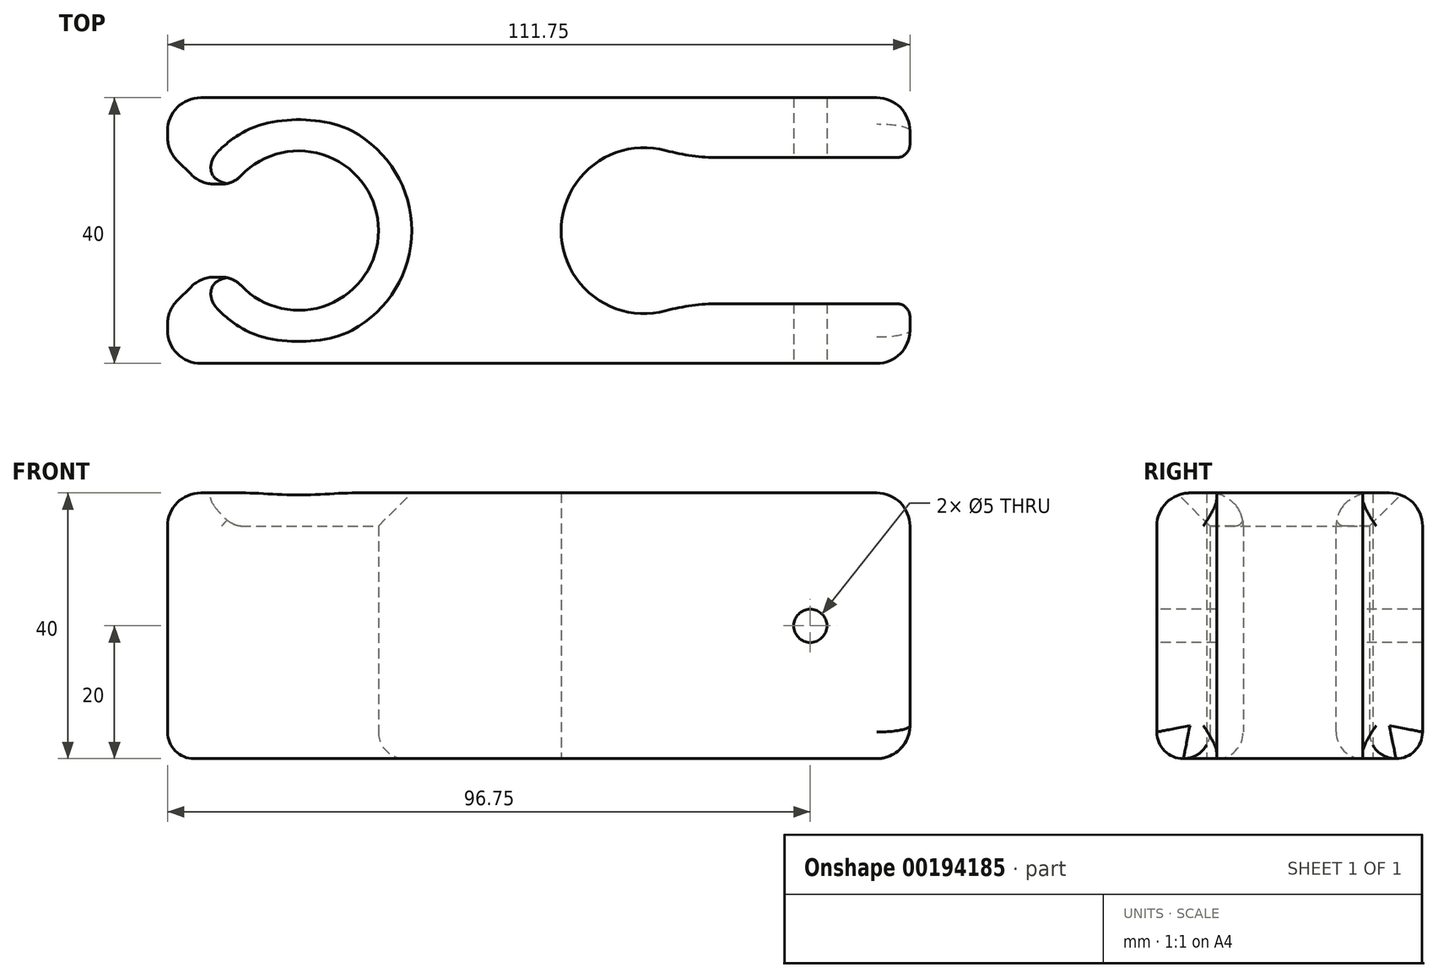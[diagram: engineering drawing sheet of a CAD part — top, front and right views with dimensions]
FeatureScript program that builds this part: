
annotation { "Feature Type Name" : "Feature", "Feature Type Description" : "" }
export const myFeature = defineFeature(function(context is Context, id is Id, definition is map)
    precondition{}
    {
        {
            var Q0;
            Q0=qCreatedBy(makeId("Top.planeOp"),FACE);
            var sketch = newSketch(context, id + "F0", { "sketchPlane" : qUnion([Q0])});
            skArc(sketch, "E0", {"start": v(5.94, 11) * mm, "mid": v(-12.5, 0) * mm, "end": v(5.94, -11) * mm});
            skLineSegment(sketch, "E1", {"start": v(0, 20) * mm, "end": v(40, 20) * mm});
            skLineSegment(sketch, "E2", {"start": v(40, 20) * mm, "end": v(40, 11) * mm});
            skLineSegment(sketch, "E3", {"start": v(40, 11) * mm, "end": v(5.94, 11) * mm});
            skLineSegment(sketch, "E4.MirrorCS", {"start": v(0, -20) * mm, "end": v(40, -20) * mm});
            skLineSegment(sketch, "E5.MirrorCS", {"start": v(40, -20) * mm, "end": v(40, -11) * mm});
            skLineSegment(sketch, "E6.MirrorCS", {"start": v(40, -11) * mm, "end": v(5.94, -11) * mm});
            skLineSegment(sketch, "E7", {"start": v(0, 20) * mm, "end": v(-61.8, 20) * mm});
            skLineSegment(sketch, "E8", {"start": v(-64, -20) * mm, "end": v(0, -20) * mm});
            skArc(sketch, "E9", {"start": v(-61.75, -7) * mm, "mid": v(-40, 0) * mm, "end": v(-61.75, 7) * mm});
            skLineSegment(sketch, "E10", {"start": v(-61.75, 20) * mm, "end": v(-71.75, 20) * mm});
            skLineSegment(sketch, "E11", {"start": v(-71.75, -20) * mm, "end": v(-64, -20) * mm});
            skLineSegment(sketch, "E12", {"start": v(-71.75, 7) * mm, "end": v(-61.75, 7) * mm});
            skLineSegment(sketch, "E13", {"start": v(-71.75, -7) * mm, "end": v(-61.75, -7) * mm});
            skLineSegment(sketch, "E14", {"start": v(-71.75, 7) * mm, "end": v(-71.75, 20) * mm});
            skLineSegment(sketch, "E15", {"start": v(-71.75, -20) * mm, "end": v(-71.75, -7) * mm});
            skSolve(sketch);
        }
        {
            var Q0;
            Q0=makeQuery(id+"F0.imprint","IMPRINT",FACE,{"disambiguationData":[TD([[makeQuery(id+"F0.imprint","IMPRINT",EDGE,{"derivedFrom":sQuery(id+"F0.wireOp",EDGE,"E0")}),-1.0]])]});
            extrude(context, id + "F1", {"entities" : qUnion([Q0]), "depth" : 40 * mm});
        }
        {
            var Q0;
            Q0=makeQuery(id+"F1.opExtrude","SWEPT_EDGE",EDGE,{"disambiguationData":[OSD([sQuery(id+"F0.wireOp",EDGE,"E9"),sQuery(id+"F0.wireOp",EDGE,"E12")])]});
            var Q1;
            Q1=makeQuery(id+"F1.opExtrude","SWEPT_EDGE",EDGE,{"disambiguationData":[OSD([sQuery(id+"F0.wireOp",EDGE,"E9"),sQuery(id+"F0.wireOp",EDGE,"E13")])]});
            fillet(context, id + "F2", {"entities" : qUnion([Q0, Q1]), "radius" : 4 * mm, "tangentPropagation" : true, "allowEdgeOverflow" : false});
        }
        {
            var Q0;
            Q0=makeQuery(id+"F1.opExtrude","SWEPT_EDGE",EDGE,{"disambiguationData":[OSD([sQuery(id+"F0.wireOp",EDGE,"E12"),sQuery(id+"F0.wireOp",EDGE,"E14")])]});
            var Q1;
            Q1=makeQuery(id+"F1.opExtrude","SWEPT_EDGE",EDGE,{"disambiguationData":[OSD([sQuery(id+"F0.wireOp",EDGE,"E13"),sQuery(id+"F0.wireOp",EDGE,"E15")])]});
            chamfer(context, id + "F3", {"entities" : qUnion([Q0, Q1]), "width" : 5 * mm, "tangentPropagation" : true});
        }
        {
            var Q0;
            {var subQ0=sQuery(id+"F0.wireOp",EDGE,"E12");Q0=makeQuery(id+"F3.opChamfer","BLEND_EDGE",EDGE,{"blendedFrom":[makeQuery(id+"F1.opExtrude","SWEPT_EDGE",EDGE,{"disambiguationData":[OSD([subQ0,sQuery(id+"F0.wireOp",EDGE,"E14")])]}),makeQuery(id+"F1.opExtrude","SWEPT_FACE",FACE,{"disambiguationData":[OSD([subQ0])]})],"blendedInto":[makeQuery(id+"F1.opExtrude","SWEPT_FACE",FACE,{"disambiguationData":[OSD([subQ0])]})]});}
            var Q1;
            {var subQ0=sQuery(id+"F0.wireOp",EDGE,"E14");Q1=makeQuery(id+"F3.opChamfer","BLEND_EDGE",EDGE,{"blendedFrom":[makeQuery(id+"F1.opExtrude","SWEPT_EDGE",EDGE,{"disambiguationData":[OSD([sQuery(id+"F0.wireOp",EDGE,"E12"),subQ0])]}),makeQuery(id+"F1.opExtrude","SWEPT_FACE",FACE,{"disambiguationData":[OSD([subQ0])]})],"blendedInto":[makeQuery(id+"F1.opExtrude","SWEPT_FACE",FACE,{"disambiguationData":[OSD([subQ0])]})]});}
            var Q2;
            {var subQ0=sQuery(id+"F0.wireOp",EDGE,"E13");Q2=makeQuery(id+"F3.opChamfer","BLEND_EDGE",EDGE,{"blendedFrom":[makeQuery(id+"F1.opExtrude","SWEPT_EDGE",EDGE,{"disambiguationData":[OSD([subQ0,sQuery(id+"F0.wireOp",EDGE,"E15")])]}),makeQuery(id+"F1.opExtrude","SWEPT_FACE",FACE,{"disambiguationData":[OSD([subQ0])]})],"blendedInto":[makeQuery(id+"F1.opExtrude","SWEPT_FACE",FACE,{"disambiguationData":[OSD([subQ0])]})]});}
            var Q3;
            {var subQ0=sQuery(id+"F0.wireOp",EDGE,"E15");Q3=makeQuery(id+"F3.opChamfer","BLEND_EDGE",EDGE,{"blendedFrom":[makeQuery(id+"F1.opExtrude","SWEPT_EDGE",EDGE,{"disambiguationData":[OSD([sQuery(id+"F0.wireOp",EDGE,"E13"),subQ0])]}),makeQuery(id+"F1.opExtrude","SWEPT_FACE",FACE,{"disambiguationData":[OSD([subQ0])]})],"blendedInto":[makeQuery(id+"F1.opExtrude","SWEPT_FACE",FACE,{"disambiguationData":[OSD([subQ0])]})]});}
            fillet(context, id + "F4", {"entities" : qUnion([Q0, Q1, Q2, Q3]), "radius" : 5 * mm, "tangentPropagation" : true, "allowEdgeOverflow" : false});
        }
        {
            var Q0;
            Q0=makeQuery(id+"F1.opExtrude","SWEPT_EDGE",EDGE,{"disambiguationData":[OSD([sQuery(id+"F0.wireOp",EDGE,"E10"),sQuery(id+"F0.wireOp",EDGE,"E14")])]});
            var Q1;
            Q1=makeQuery(id+"F1.opExtrude","SWEPT_EDGE",EDGE,{"disambiguationData":[OSD([sQuery(id+"F0.wireOp",EDGE,"E11"),sQuery(id+"F0.wireOp",EDGE,"E15")])]});
            fillet(context, id + "F5", {"entities" : qUnion([Q0, Q1]), "radius" : 5 * mm, "tangentPropagation" : true, "allowEdgeOverflow" : false});
        }
        {
            var Q0;
            Q0=makeQuery(id+"F1.opExtrude","SWEPT_EDGE",EDGE,{"disambiguationData":[OSD([sQuery(id+"F0.wireOp",EDGE,"E2"),sQuery(id+"F0.wireOp",EDGE,"E3")])]});
            fillet(context, id + "F6", {"entities" : qUnion([Q0]), "radius" : 2 * mm, "tangentPropagation" : true, "allowEdgeOverflow" : false});
        }
        {
            var Q0;
            Q0=makeQuery(id+"F1.opExtrude","SWEPT_EDGE",EDGE,{"disambiguationData":[OSD([sQuery(id+"F0.wireOp",EDGE,"E5.MirrorCS"),sQuery(id+"F0.wireOp",EDGE,"E6.MirrorCS")])]});
            fillet(context, id + "F7", {"entities" : qUnion([Q0]), "radius" : 2 * mm, "tangentPropagation" : true, "allowEdgeOverflow" : false});
        }
        {
            var Q0;
            Q0=makeQuery(id+"F1.opExtrude","CAP_EDGE",EDGE,{"disambiguationData":[OSD([sQuery(id+"F0.wireOp",EDGE,"E4.MirrorCS"),sQuery(id+"F0.wireOp",EDGE,"E8"),sQuery(id+"F0.wireOp",EDGE,"E11")])],"isStart":true});
            fillet(context, id + "F8", {"entities" : qUnion([Q0]), "radius" : 4 * mm, "tangentPropagation" : true, "allowEdgeOverflow" : false});
        }
        {
            var Q0;
            Q0=makeQuery(id+"F1.opExtrude","SWEPT_EDGE",EDGE,{"disambiguationData":[OSD([sQuery(id+"F0.wireOp",EDGE,"E0"),sQuery(id+"F0.wireOp",EDGE,"E3")])]});
            var Q1;
            Q1=makeQuery(id+"F1.opExtrude","SWEPT_EDGE",EDGE,{"disambiguationData":[OSD([sQuery(id+"F0.wireOp",EDGE,"E0"),sQuery(id+"F0.wireOp",EDGE,"E6.MirrorCS")])]});
            fillet(context, id + "F9", {"entities" : qUnion([Q0, Q1]), "radius" : 30 * mm, "tangentPropagation" : true, "allowEdgeOverflow" : false});
        }
        {
            var Q0;
            Q0=makeQuery(id+"F1.opExtrude","SWEPT_FACE",FACE,{"disambiguationData":[OSD([sQuery(id+"F0.wireOp",EDGE,"E4.MirrorCS"),sQuery(id+"F0.wireOp",EDGE,"E8"),sQuery(id+"F0.wireOp",EDGE,"E11")])]});
            var sketch = newSketch(context, id + "F10", { "sketchPlane" : qUnion([Q0])});
            skLineSegment(sketch, "E16.bottom", {"start": v(40, 36) * mm, "end": v(10, 36) * mm});
            skLineSegment(sketch, "E16.top", {"start": v(40, 4) * mm, "end": v(10, 4) * mm});
            skLineSegment(sketch, "E16.left", {"start": v(40, 36) * mm, "end": v(40, 4) * mm});
            skLineSegment(sketch, "E16.right", {"start": v(10, 36) * mm, "end": v(10, 4) * mm});
            skLineSegment(sketch, "E17", {"start": v(10, 36) * mm, "end": v(40, 4) * mm});
            skLineSegment(sketch, "E18", {"start": v(40, 36) * mm, "end": v(10, 4) * mm});
            skLineSegment(sketch, "E19.bottom", {"start": v(25, 20) * mm, "end": v(31.34, 20) * mm});
            skLineSegment(sketch, "E19.top", {"start": v(25, 15.25) * mm, "end": v(31.34, 15.25) * mm});
            skLineSegment(sketch, "E19.left", {"start": v(25, 20) * mm, "end": v(25, 15.25) * mm});
            skLineSegment(sketch, "E19.right", {"start": v(31.34, 20) * mm, "end": v(31.34, 15.25) * mm});
            skSolve(sketch);
        }
        {
            var Q0;
            Q0=sQuery(id+"F10.wireOp",VERTEX,"E19.left.start");
            var Q1;
            Q1=makeQuery(id+"F1.opExtrude","SWEPT_BODY",BODY,{"disambiguationData":[OSD([sQuery(id+"F0.wireOp",EDGE,"E0"),sQuery(id+"F0.wireOp",EDGE,"E1"),sQuery(id+"F0.wireOp",EDGE,"E2"),sQuery(id+"F0.wireOp",EDGE,"E3"),sQuery(id+"F0.wireOp",EDGE,"E4.MirrorCS"),sQuery(id+"F0.wireOp",EDGE,"E5.MirrorCS"),sQuery(id+"F0.wireOp",EDGE,"E6.MirrorCS"),sQuery(id+"F0.wireOp",EDGE,"E7"),sQuery(id+"F0.wireOp",EDGE,"E8"),sQuery(id+"F0.wireOp",EDGE,"E9"),sQuery(id+"F0.wireOp",EDGE,"E10"),sQuery(id+"F0.wireOp",EDGE,"E11"),sQuery(id+"F0.wireOp",EDGE,"E12"),sQuery(id+"F0.wireOp",EDGE,"E13"),sQuery(id+"F0.wireOp",EDGE,"E14"),sQuery(id+"F0.wireOp",EDGE,"E15")])]});
            hole(context, id + "F11", {"style" : HoleStyle.SIMPLE, "endStyle" : HoleEndStyle.THROUGH, "holeDiameter" : 5 * mm, "startFromSketch" : true, "locations" : qUnion([Q0]), "scope" : qUnion([Q1]), "isTappedThrough" : true});
        }
        {
            var Q0;
            Q0=makeQuery(id+"F1.opExtrude","SWEPT_EDGE",EDGE,{"disambiguationData":[OSD([sQuery(id+"F0.wireOp",EDGE,"E4.MirrorCS"),sQuery(id+"F0.wireOp",EDGE,"E5.MirrorCS")])]});
            fillet(context, id + "F12", {"entities" : qUnion([Q0]), "radius" : 5 * mm, "allowEdgeOverflow" : false});
        }
        {
            var Q0;
            Q0=makeQuery(id+"F1.opExtrude","SWEPT_EDGE",EDGE,{"disambiguationData":[OSD([sQuery(id+"F0.wireOp",EDGE,"E1"),sQuery(id+"F0.wireOp",EDGE,"E2")])]});
            fillet(context, id + "F13", {"entities" : qUnion([Q0]), "radius" : 5 * mm, "allowEdgeOverflow" : false});
        }
        {
            var Q0;
            Q0=makeQuery(id+"F1.opExtrude","CAP_EDGE",EDGE,{"disambiguationData":[OSD([sQuery(id+"F0.wireOp",EDGE,"E9")])],"isStart":false});
            chamfer(context, id + "F14", {"entities" : qUnion([Q0]), "width" : 5 * mm});
        }
        {
            var Q0;
            Q0=makeQuery(id+"F1.opExtrude","CAP_EDGE",EDGE,{"disambiguationData":[OSD([sQuery(id+"F0.wireOp",EDGE,"E4.MirrorCS"),sQuery(id+"F0.wireOp",EDGE,"E8"),sQuery(id+"F0.wireOp",EDGE,"E11")])],"isStart":false});
            var Q1;
            {var subQ0=sQuery(id+"F0.wireOp",EDGE,"E5.MirrorCS");var subQ1=sQuery(id+"F0.wireOp",EDGE,"E4.MirrorCS");Q1=makeQuery(id+"F12.opFillet","BLEND_EDGE",EDGE,{"blendedFrom":[makeQuery(id+"F1.opExtrude","SWEPT_EDGE",EDGE,{"disambiguationData":[OSD([subQ1,subQ0])]}),makeQuery(id+"F1.opExtrude","CAP_FACE",FACE,{"disambiguationData":[OSD([sQuery(id+"F0.wireOp",EDGE,"E0"),sQuery(id+"F0.wireOp",EDGE,"E1"),sQuery(id+"F0.wireOp",EDGE,"E2"),sQuery(id+"F0.wireOp",EDGE,"E3"),subQ1,subQ0,sQuery(id+"F0.wireOp",EDGE,"E6.MirrorCS"),sQuery(id+"F0.wireOp",EDGE,"E7"),sQuery(id+"F0.wireOp",EDGE,"E8"),sQuery(id+"F0.wireOp",EDGE,"E9"),sQuery(id+"F0.wireOp",EDGE,"E10"),sQuery(id+"F0.wireOp",EDGE,"E11"),sQuery(id+"F0.wireOp",EDGE,"E12"),sQuery(id+"F0.wireOp",EDGE,"E13"),sQuery(id+"F0.wireOp",EDGE,"E14"),sQuery(id+"F0.wireOp",EDGE,"E15")])],"isStart":false})],"blendedInto":[makeQuery(id+"F1.opExtrude","CAP_FACE",FACE,{"disambiguationData":[OSD([sQuery(id+"F0.wireOp",EDGE,"E0"),sQuery(id+"F0.wireOp",EDGE,"E1"),sQuery(id+"F0.wireOp",EDGE,"E2"),sQuery(id+"F0.wireOp",EDGE,"E3"),subQ1,subQ0,sQuery(id+"F0.wireOp",EDGE,"E6.MirrorCS"),sQuery(id+"F0.wireOp",EDGE,"E7"),sQuery(id+"F0.wireOp",EDGE,"E8"),sQuery(id+"F0.wireOp",EDGE,"E9"),sQuery(id+"F0.wireOp",EDGE,"E10"),sQuery(id+"F0.wireOp",EDGE,"E11"),sQuery(id+"F0.wireOp",EDGE,"E12"),sQuery(id+"F0.wireOp",EDGE,"E13"),sQuery(id+"F0.wireOp",EDGE,"E14"),sQuery(id+"F0.wireOp",EDGE,"E15")])],"isStart":false})]});}
            var Q2;
            Q2=makeQuery(id+"F1.opExtrude","CAP_EDGE",EDGE,{"disambiguationData":[OSD([sQuery(id+"F0.wireOp",EDGE,"E5.MirrorCS")])],"isStart":false});
            var Q3;
            {var subQ0=sQuery(id+"F0.wireOp",EDGE,"E6.MirrorCS");var subQ1=sQuery(id+"F0.wireOp",EDGE,"E5.MirrorCS");Q3=makeQuery(id+"F7.opFillet","BLEND_EDGE",EDGE,{"blendedFrom":[makeQuery(id+"F1.opExtrude","SWEPT_EDGE",EDGE,{"disambiguationData":[OSD([subQ1,subQ0])]}),makeQuery(id+"F1.opExtrude","CAP_FACE",FACE,{"disambiguationData":[OSD([sQuery(id+"F0.wireOp",EDGE,"E0"),sQuery(id+"F0.wireOp",EDGE,"E1"),sQuery(id+"F0.wireOp",EDGE,"E2"),sQuery(id+"F0.wireOp",EDGE,"E3"),sQuery(id+"F0.wireOp",EDGE,"E4.MirrorCS"),subQ1,subQ0,sQuery(id+"F0.wireOp",EDGE,"E7"),sQuery(id+"F0.wireOp",EDGE,"E8"),sQuery(id+"F0.wireOp",EDGE,"E9"),sQuery(id+"F0.wireOp",EDGE,"E10"),sQuery(id+"F0.wireOp",EDGE,"E11"),sQuery(id+"F0.wireOp",EDGE,"E12"),sQuery(id+"F0.wireOp",EDGE,"E13"),sQuery(id+"F0.wireOp",EDGE,"E14"),sQuery(id+"F0.wireOp",EDGE,"E15")])],"isStart":false})],"blendedInto":[makeQuery(id+"F1.opExtrude","CAP_FACE",FACE,{"disambiguationData":[OSD([sQuery(id+"F0.wireOp",EDGE,"E0"),sQuery(id+"F0.wireOp",EDGE,"E1"),sQuery(id+"F0.wireOp",EDGE,"E2"),sQuery(id+"F0.wireOp",EDGE,"E3"),sQuery(id+"F0.wireOp",EDGE,"E4.MirrorCS"),subQ1,subQ0,sQuery(id+"F0.wireOp",EDGE,"E7"),sQuery(id+"F0.wireOp",EDGE,"E8"),sQuery(id+"F0.wireOp",EDGE,"E9"),sQuery(id+"F0.wireOp",EDGE,"E10"),sQuery(id+"F0.wireOp",EDGE,"E11"),sQuery(id+"F0.wireOp",EDGE,"E12"),sQuery(id+"F0.wireOp",EDGE,"E13"),sQuery(id+"F0.wireOp",EDGE,"E14"),sQuery(id+"F0.wireOp",EDGE,"E15")])],"isStart":false})]});}
            var Q4;
            {var subQ0=sQuery(id+"F0.wireOp",EDGE,"E3");var subQ1=sQuery(id+"F0.wireOp",EDGE,"E2");Q4=makeQuery(id+"F6.opFillet","BLEND_EDGE",EDGE,{"blendedFrom":[makeQuery(id+"F1.opExtrude","SWEPT_EDGE",EDGE,{"disambiguationData":[OSD([subQ1,subQ0])]}),makeQuery(id+"F1.opExtrude","CAP_FACE",FACE,{"disambiguationData":[OSD([sQuery(id+"F0.wireOp",EDGE,"E0"),sQuery(id+"F0.wireOp",EDGE,"E1"),subQ1,subQ0,sQuery(id+"F0.wireOp",EDGE,"E4.MirrorCS"),sQuery(id+"F0.wireOp",EDGE,"E5.MirrorCS"),sQuery(id+"F0.wireOp",EDGE,"E6.MirrorCS"),sQuery(id+"F0.wireOp",EDGE,"E7"),sQuery(id+"F0.wireOp",EDGE,"E8"),sQuery(id+"F0.wireOp",EDGE,"E9"),sQuery(id+"F0.wireOp",EDGE,"E10"),sQuery(id+"F0.wireOp",EDGE,"E11"),sQuery(id+"F0.wireOp",EDGE,"E12"),sQuery(id+"F0.wireOp",EDGE,"E13"),sQuery(id+"F0.wireOp",EDGE,"E14"),sQuery(id+"F0.wireOp",EDGE,"E15")])],"isStart":false})],"blendedInto":[makeQuery(id+"F1.opExtrude","CAP_FACE",FACE,{"disambiguationData":[OSD([sQuery(id+"F0.wireOp",EDGE,"E0"),sQuery(id+"F0.wireOp",EDGE,"E1"),subQ1,subQ0,sQuery(id+"F0.wireOp",EDGE,"E4.MirrorCS"),sQuery(id+"F0.wireOp",EDGE,"E5.MirrorCS"),sQuery(id+"F0.wireOp",EDGE,"E6.MirrorCS"),sQuery(id+"F0.wireOp",EDGE,"E7"),sQuery(id+"F0.wireOp",EDGE,"E8"),sQuery(id+"F0.wireOp",EDGE,"E9"),sQuery(id+"F0.wireOp",EDGE,"E10"),sQuery(id+"F0.wireOp",EDGE,"E11"),sQuery(id+"F0.wireOp",EDGE,"E12"),sQuery(id+"F0.wireOp",EDGE,"E13"),sQuery(id+"F0.wireOp",EDGE,"E14"),sQuery(id+"F0.wireOp",EDGE,"E15")])],"isStart":false})]});}
            var Q5;
            Q5=makeQuery(id+"F1.opExtrude","CAP_EDGE",EDGE,{"disambiguationData":[OSD([sQuery(id+"F0.wireOp",EDGE,"E2")])],"isStart":false});
            var Q6;
            {var subQ0=sQuery(id+"F0.wireOp",EDGE,"E2");var subQ1=sQuery(id+"F0.wireOp",EDGE,"E1");Q6=makeQuery(id+"F13.opFillet","BLEND_EDGE",EDGE,{"blendedFrom":[makeQuery(id+"F1.opExtrude","SWEPT_EDGE",EDGE,{"disambiguationData":[OSD([subQ1,subQ0])]}),makeQuery(id+"F1.opExtrude","CAP_FACE",FACE,{"disambiguationData":[OSD([sQuery(id+"F0.wireOp",EDGE,"E0"),subQ1,subQ0,sQuery(id+"F0.wireOp",EDGE,"E3"),sQuery(id+"F0.wireOp",EDGE,"E4.MirrorCS"),sQuery(id+"F0.wireOp",EDGE,"E5.MirrorCS"),sQuery(id+"F0.wireOp",EDGE,"E6.MirrorCS"),sQuery(id+"F0.wireOp",EDGE,"E7"),sQuery(id+"F0.wireOp",EDGE,"E8"),sQuery(id+"F0.wireOp",EDGE,"E9"),sQuery(id+"F0.wireOp",EDGE,"E10"),sQuery(id+"F0.wireOp",EDGE,"E11"),sQuery(id+"F0.wireOp",EDGE,"E12"),sQuery(id+"F0.wireOp",EDGE,"E13"),sQuery(id+"F0.wireOp",EDGE,"E14"),sQuery(id+"F0.wireOp",EDGE,"E15")])],"isStart":false})],"blendedInto":[makeQuery(id+"F1.opExtrude","CAP_FACE",FACE,{"disambiguationData":[OSD([sQuery(id+"F0.wireOp",EDGE,"E0"),subQ1,subQ0,sQuery(id+"F0.wireOp",EDGE,"E3"),sQuery(id+"F0.wireOp",EDGE,"E4.MirrorCS"),sQuery(id+"F0.wireOp",EDGE,"E5.MirrorCS"),sQuery(id+"F0.wireOp",EDGE,"E6.MirrorCS"),sQuery(id+"F0.wireOp",EDGE,"E7"),sQuery(id+"F0.wireOp",EDGE,"E8"),sQuery(id+"F0.wireOp",EDGE,"E9"),sQuery(id+"F0.wireOp",EDGE,"E10"),sQuery(id+"F0.wireOp",EDGE,"E11"),sQuery(id+"F0.wireOp",EDGE,"E12"),sQuery(id+"F0.wireOp",EDGE,"E13"),sQuery(id+"F0.wireOp",EDGE,"E14"),sQuery(id+"F0.wireOp",EDGE,"E15")])],"isStart":false})]});}
            var Q7;
            Q7=makeQuery(id+"F1.opExtrude","CAP_EDGE",EDGE,{"disambiguationData":[OSD([sQuery(id+"F0.wireOp",EDGE,"E1"),sQuery(id+"F0.wireOp",EDGE,"E7"),sQuery(id+"F0.wireOp",EDGE,"E10")])],"isStart":false});
            var Q8;
            {var subQ0=sQuery(id+"F0.wireOp",EDGE,"E14");var subQ1=sQuery(id+"F0.wireOp",EDGE,"E10");Q8=makeQuery(id+"F5.opFillet","BLEND_EDGE",EDGE,{"blendedFrom":[makeQuery(id+"F1.opExtrude","SWEPT_EDGE",EDGE,{"disambiguationData":[OSD([subQ1,subQ0])]}),makeQuery(id+"F1.opExtrude","CAP_FACE",FACE,{"disambiguationData":[OSD([sQuery(id+"F0.wireOp",EDGE,"E0"),sQuery(id+"F0.wireOp",EDGE,"E1"),sQuery(id+"F0.wireOp",EDGE,"E2"),sQuery(id+"F0.wireOp",EDGE,"E3"),sQuery(id+"F0.wireOp",EDGE,"E4.MirrorCS"),sQuery(id+"F0.wireOp",EDGE,"E5.MirrorCS"),sQuery(id+"F0.wireOp",EDGE,"E6.MirrorCS"),sQuery(id+"F0.wireOp",EDGE,"E7"),sQuery(id+"F0.wireOp",EDGE,"E8"),sQuery(id+"F0.wireOp",EDGE,"E9"),subQ1,sQuery(id+"F0.wireOp",EDGE,"E11"),sQuery(id+"F0.wireOp",EDGE,"E12"),sQuery(id+"F0.wireOp",EDGE,"E13"),subQ0,sQuery(id+"F0.wireOp",EDGE,"E15")])],"isStart":false})],"blendedInto":[makeQuery(id+"F1.opExtrude","CAP_FACE",FACE,{"disambiguationData":[OSD([sQuery(id+"F0.wireOp",EDGE,"E0"),sQuery(id+"F0.wireOp",EDGE,"E1"),sQuery(id+"F0.wireOp",EDGE,"E2"),sQuery(id+"F0.wireOp",EDGE,"E3"),sQuery(id+"F0.wireOp",EDGE,"E4.MirrorCS"),sQuery(id+"F0.wireOp",EDGE,"E5.MirrorCS"),sQuery(id+"F0.wireOp",EDGE,"E6.MirrorCS"),sQuery(id+"F0.wireOp",EDGE,"E7"),sQuery(id+"F0.wireOp",EDGE,"E8"),sQuery(id+"F0.wireOp",EDGE,"E9"),subQ1,sQuery(id+"F0.wireOp",EDGE,"E11"),sQuery(id+"F0.wireOp",EDGE,"E12"),sQuery(id+"F0.wireOp",EDGE,"E13"),subQ0,sQuery(id+"F0.wireOp",EDGE,"E15")])],"isStart":false})]});}
            var Q9;
            {var subQ0=sQuery(id+"F0.wireOp",EDGE,"E14");var subQ1=sQuery(id+"F0.wireOp",EDGE,"E12");Q9=makeQuery(id+"F4.opFillet","BLEND_EDGE",EDGE,{"blendedFrom":[makeQuery(id+"F3.opChamfer","BLEND_EDGE",EDGE,{"blendedFrom":[makeQuery(id+"F1.opExtrude","SWEPT_EDGE",EDGE,{"disambiguationData":[OSD([subQ1,subQ0])]}),makeQuery(id+"F1.opExtrude","SWEPT_FACE",FACE,{"disambiguationData":[OSD([subQ0])]})],"blendedInto":[makeQuery(id+"F1.opExtrude","SWEPT_FACE",FACE,{"disambiguationData":[OSD([subQ0])]})]}),makeQuery(id+"F1.opExtrude","CAP_FACE",FACE,{"disambiguationData":[OSD([sQuery(id+"F0.wireOp",EDGE,"E0"),sQuery(id+"F0.wireOp",EDGE,"E1"),sQuery(id+"F0.wireOp",EDGE,"E2"),sQuery(id+"F0.wireOp",EDGE,"E3"),sQuery(id+"F0.wireOp",EDGE,"E4.MirrorCS"),sQuery(id+"F0.wireOp",EDGE,"E5.MirrorCS"),sQuery(id+"F0.wireOp",EDGE,"E6.MirrorCS"),sQuery(id+"F0.wireOp",EDGE,"E7"),sQuery(id+"F0.wireOp",EDGE,"E8"),sQuery(id+"F0.wireOp",EDGE,"E9"),sQuery(id+"F0.wireOp",EDGE,"E10"),sQuery(id+"F0.wireOp",EDGE,"E11"),subQ1,sQuery(id+"F0.wireOp",EDGE,"E13"),subQ0,sQuery(id+"F0.wireOp",EDGE,"E15")])],"isStart":false})],"blendedInto":[makeQuery(id+"F1.opExtrude","CAP_FACE",FACE,{"disambiguationData":[OSD([sQuery(id+"F0.wireOp",EDGE,"E0"),sQuery(id+"F0.wireOp",EDGE,"E1"),sQuery(id+"F0.wireOp",EDGE,"E2"),sQuery(id+"F0.wireOp",EDGE,"E3"),sQuery(id+"F0.wireOp",EDGE,"E4.MirrorCS"),sQuery(id+"F0.wireOp",EDGE,"E5.MirrorCS"),sQuery(id+"F0.wireOp",EDGE,"E6.MirrorCS"),sQuery(id+"F0.wireOp",EDGE,"E7"),sQuery(id+"F0.wireOp",EDGE,"E8"),sQuery(id+"F0.wireOp",EDGE,"E9"),sQuery(id+"F0.wireOp",EDGE,"E10"),sQuery(id+"F0.wireOp",EDGE,"E11"),subQ1,sQuery(id+"F0.wireOp",EDGE,"E13"),subQ0,sQuery(id+"F0.wireOp",EDGE,"E15")])],"isStart":false})]});}
            var Q10;
            Q10=makeQuery(id+"F1.opExtrude","CAP_EDGE",EDGE,{"disambiguationData":[OSD([sQuery(id+"F0.wireOp",EDGE,"E14")])],"isStart":false});
            var Q11;
            {var subQ0=sQuery(id+"F0.wireOp",EDGE,"E14");var subQ1=sQuery(id+"F0.wireOp",EDGE,"E12");Q11=makeQuery(id+"F3.opChamfer","BLEND_EDGE",EDGE,{"blendedFrom":[makeQuery(id+"F1.opExtrude","SWEPT_EDGE",EDGE,{"disambiguationData":[OSD([subQ1,subQ0])]}),makeQuery(id+"F1.opExtrude","CAP_FACE",FACE,{"disambiguationData":[OSD([sQuery(id+"F0.wireOp",EDGE,"E0"),sQuery(id+"F0.wireOp",EDGE,"E1"),sQuery(id+"F0.wireOp",EDGE,"E2"),sQuery(id+"F0.wireOp",EDGE,"E3"),sQuery(id+"F0.wireOp",EDGE,"E4.MirrorCS"),sQuery(id+"F0.wireOp",EDGE,"E5.MirrorCS"),sQuery(id+"F0.wireOp",EDGE,"E6.MirrorCS"),sQuery(id+"F0.wireOp",EDGE,"E7"),sQuery(id+"F0.wireOp",EDGE,"E8"),sQuery(id+"F0.wireOp",EDGE,"E9"),sQuery(id+"F0.wireOp",EDGE,"E10"),sQuery(id+"F0.wireOp",EDGE,"E11"),subQ1,sQuery(id+"F0.wireOp",EDGE,"E13"),subQ0,sQuery(id+"F0.wireOp",EDGE,"E15")])],"isStart":false})],"blendedInto":[makeQuery(id+"F1.opExtrude","CAP_FACE",FACE,{"disambiguationData":[OSD([sQuery(id+"F0.wireOp",EDGE,"E0"),sQuery(id+"F0.wireOp",EDGE,"E1"),sQuery(id+"F0.wireOp",EDGE,"E2"),sQuery(id+"F0.wireOp",EDGE,"E3"),sQuery(id+"F0.wireOp",EDGE,"E4.MirrorCS"),sQuery(id+"F0.wireOp",EDGE,"E5.MirrorCS"),sQuery(id+"F0.wireOp",EDGE,"E6.MirrorCS"),sQuery(id+"F0.wireOp",EDGE,"E7"),sQuery(id+"F0.wireOp",EDGE,"E8"),sQuery(id+"F0.wireOp",EDGE,"E9"),sQuery(id+"F0.wireOp",EDGE,"E10"),sQuery(id+"F0.wireOp",EDGE,"E11"),subQ1,sQuery(id+"F0.wireOp",EDGE,"E13"),subQ0,sQuery(id+"F0.wireOp",EDGE,"E15")])],"isStart":false})]});}
            var Q12;
            {var subQ0=sQuery(id+"F0.wireOp",EDGE,"E14");var subQ1=sQuery(id+"F0.wireOp",EDGE,"E12");Q12=makeQuery(id+"F4.opFillet","BLEND_EDGE",EDGE,{"blendedFrom":[makeQuery(id+"F3.opChamfer","BLEND_EDGE",EDGE,{"blendedFrom":[makeQuery(id+"F1.opExtrude","SWEPT_EDGE",EDGE,{"disambiguationData":[OSD([subQ1,subQ0])]}),makeQuery(id+"F1.opExtrude","SWEPT_FACE",FACE,{"disambiguationData":[OSD([subQ1])]})],"blendedInto":[makeQuery(id+"F1.opExtrude","SWEPT_FACE",FACE,{"disambiguationData":[OSD([subQ1])]})]}),makeQuery(id+"F1.opExtrude","CAP_FACE",FACE,{"disambiguationData":[OSD([sQuery(id+"F0.wireOp",EDGE,"E0"),sQuery(id+"F0.wireOp",EDGE,"E1"),sQuery(id+"F0.wireOp",EDGE,"E2"),sQuery(id+"F0.wireOp",EDGE,"E3"),sQuery(id+"F0.wireOp",EDGE,"E4.MirrorCS"),sQuery(id+"F0.wireOp",EDGE,"E5.MirrorCS"),sQuery(id+"F0.wireOp",EDGE,"E6.MirrorCS"),sQuery(id+"F0.wireOp",EDGE,"E7"),sQuery(id+"F0.wireOp",EDGE,"E8"),sQuery(id+"F0.wireOp",EDGE,"E9"),sQuery(id+"F0.wireOp",EDGE,"E10"),sQuery(id+"F0.wireOp",EDGE,"E11"),subQ1,sQuery(id+"F0.wireOp",EDGE,"E13"),subQ0,sQuery(id+"F0.wireOp",EDGE,"E15")])],"isStart":false})],"blendedInto":[makeQuery(id+"F1.opExtrude","CAP_FACE",FACE,{"disambiguationData":[OSD([sQuery(id+"F0.wireOp",EDGE,"E0"),sQuery(id+"F0.wireOp",EDGE,"E1"),sQuery(id+"F0.wireOp",EDGE,"E2"),sQuery(id+"F0.wireOp",EDGE,"E3"),sQuery(id+"F0.wireOp",EDGE,"E4.MirrorCS"),sQuery(id+"F0.wireOp",EDGE,"E5.MirrorCS"),sQuery(id+"F0.wireOp",EDGE,"E6.MirrorCS"),sQuery(id+"F0.wireOp",EDGE,"E7"),sQuery(id+"F0.wireOp",EDGE,"E8"),sQuery(id+"F0.wireOp",EDGE,"E9"),sQuery(id+"F0.wireOp",EDGE,"E10"),sQuery(id+"F0.wireOp",EDGE,"E11"),subQ1,sQuery(id+"F0.wireOp",EDGE,"E13"),subQ0,sQuery(id+"F0.wireOp",EDGE,"E15")])],"isStart":false})]});}
            var Q13;
            {var subQ0=sQuery(id+"F0.wireOp",EDGE,"E15");var subQ1=sQuery(id+"F0.wireOp",EDGE,"E11");Q13=makeQuery(id+"F5.opFillet","BLEND_EDGE",EDGE,{"blendedFrom":[makeQuery(id+"F1.opExtrude","SWEPT_EDGE",EDGE,{"disambiguationData":[OSD([subQ1,subQ0])]}),makeQuery(id+"F1.opExtrude","CAP_FACE",FACE,{"disambiguationData":[OSD([sQuery(id+"F0.wireOp",EDGE,"E0"),sQuery(id+"F0.wireOp",EDGE,"E1"),sQuery(id+"F0.wireOp",EDGE,"E2"),sQuery(id+"F0.wireOp",EDGE,"E3"),sQuery(id+"F0.wireOp",EDGE,"E4.MirrorCS"),sQuery(id+"F0.wireOp",EDGE,"E5.MirrorCS"),sQuery(id+"F0.wireOp",EDGE,"E6.MirrorCS"),sQuery(id+"F0.wireOp",EDGE,"E7"),sQuery(id+"F0.wireOp",EDGE,"E8"),sQuery(id+"F0.wireOp",EDGE,"E9"),sQuery(id+"F0.wireOp",EDGE,"E10"),subQ1,sQuery(id+"F0.wireOp",EDGE,"E12"),sQuery(id+"F0.wireOp",EDGE,"E13"),sQuery(id+"F0.wireOp",EDGE,"E14"),subQ0])],"isStart":false})],"blendedInto":[makeQuery(id+"F1.opExtrude","CAP_FACE",FACE,{"disambiguationData":[OSD([sQuery(id+"F0.wireOp",EDGE,"E0"),sQuery(id+"F0.wireOp",EDGE,"E1"),sQuery(id+"F0.wireOp",EDGE,"E2"),sQuery(id+"F0.wireOp",EDGE,"E3"),sQuery(id+"F0.wireOp",EDGE,"E4.MirrorCS"),sQuery(id+"F0.wireOp",EDGE,"E5.MirrorCS"),sQuery(id+"F0.wireOp",EDGE,"E6.MirrorCS"),sQuery(id+"F0.wireOp",EDGE,"E7"),sQuery(id+"F0.wireOp",EDGE,"E8"),sQuery(id+"F0.wireOp",EDGE,"E9"),sQuery(id+"F0.wireOp",EDGE,"E10"),subQ1,sQuery(id+"F0.wireOp",EDGE,"E12"),sQuery(id+"F0.wireOp",EDGE,"E13"),sQuery(id+"F0.wireOp",EDGE,"E14"),subQ0])],"isStart":false})]});}
            var Q14;
            Q14=makeQuery(id+"F1.opExtrude","CAP_EDGE",EDGE,{"disambiguationData":[OSD([sQuery(id+"F0.wireOp",EDGE,"E15")])],"isStart":false});
            var Q15;
            {var subQ0=sQuery(id+"F0.wireOp",EDGE,"E15");var subQ1=sQuery(id+"F0.wireOp",EDGE,"E13");Q15=makeQuery(id+"F4.opFillet","BLEND_EDGE",EDGE,{"blendedFrom":[makeQuery(id+"F3.opChamfer","BLEND_EDGE",EDGE,{"blendedFrom":[makeQuery(id+"F1.opExtrude","SWEPT_EDGE",EDGE,{"disambiguationData":[OSD([subQ1,subQ0])]}),makeQuery(id+"F1.opExtrude","SWEPT_FACE",FACE,{"disambiguationData":[OSD([subQ0])]})],"blendedInto":[makeQuery(id+"F1.opExtrude","SWEPT_FACE",FACE,{"disambiguationData":[OSD([subQ0])]})]}),makeQuery(id+"F1.opExtrude","CAP_FACE",FACE,{"disambiguationData":[OSD([sQuery(id+"F0.wireOp",EDGE,"E0"),sQuery(id+"F0.wireOp",EDGE,"E1"),sQuery(id+"F0.wireOp",EDGE,"E2"),sQuery(id+"F0.wireOp",EDGE,"E3"),sQuery(id+"F0.wireOp",EDGE,"E4.MirrorCS"),sQuery(id+"F0.wireOp",EDGE,"E5.MirrorCS"),sQuery(id+"F0.wireOp",EDGE,"E6.MirrorCS"),sQuery(id+"F0.wireOp",EDGE,"E7"),sQuery(id+"F0.wireOp",EDGE,"E8"),sQuery(id+"F0.wireOp",EDGE,"E9"),sQuery(id+"F0.wireOp",EDGE,"E10"),sQuery(id+"F0.wireOp",EDGE,"E11"),sQuery(id+"F0.wireOp",EDGE,"E12"),subQ1,sQuery(id+"F0.wireOp",EDGE,"E14"),subQ0])],"isStart":false})],"blendedInto":[makeQuery(id+"F1.opExtrude","CAP_FACE",FACE,{"disambiguationData":[OSD([sQuery(id+"F0.wireOp",EDGE,"E0"),sQuery(id+"F0.wireOp",EDGE,"E1"),sQuery(id+"F0.wireOp",EDGE,"E2"),sQuery(id+"F0.wireOp",EDGE,"E3"),sQuery(id+"F0.wireOp",EDGE,"E4.MirrorCS"),sQuery(id+"F0.wireOp",EDGE,"E5.MirrorCS"),sQuery(id+"F0.wireOp",EDGE,"E6.MirrorCS"),sQuery(id+"F0.wireOp",EDGE,"E7"),sQuery(id+"F0.wireOp",EDGE,"E8"),sQuery(id+"F0.wireOp",EDGE,"E9"),sQuery(id+"F0.wireOp",EDGE,"E10"),sQuery(id+"F0.wireOp",EDGE,"E11"),sQuery(id+"F0.wireOp",EDGE,"E12"),subQ1,sQuery(id+"F0.wireOp",EDGE,"E14"),subQ0])],"isStart":false})]});}
            var Q16;
            {var subQ0=sQuery(id+"F0.wireOp",EDGE,"E15");var subQ1=sQuery(id+"F0.wireOp",EDGE,"E13");Q16=makeQuery(id+"F3.opChamfer","BLEND_EDGE",EDGE,{"blendedFrom":[makeQuery(id+"F1.opExtrude","SWEPT_EDGE",EDGE,{"disambiguationData":[OSD([subQ1,subQ0])]}),makeQuery(id+"F1.opExtrude","CAP_FACE",FACE,{"disambiguationData":[OSD([sQuery(id+"F0.wireOp",EDGE,"E0"),sQuery(id+"F0.wireOp",EDGE,"E1"),sQuery(id+"F0.wireOp",EDGE,"E2"),sQuery(id+"F0.wireOp",EDGE,"E3"),sQuery(id+"F0.wireOp",EDGE,"E4.MirrorCS"),sQuery(id+"F0.wireOp",EDGE,"E5.MirrorCS"),sQuery(id+"F0.wireOp",EDGE,"E6.MirrorCS"),sQuery(id+"F0.wireOp",EDGE,"E7"),sQuery(id+"F0.wireOp",EDGE,"E8"),sQuery(id+"F0.wireOp",EDGE,"E9"),sQuery(id+"F0.wireOp",EDGE,"E10"),sQuery(id+"F0.wireOp",EDGE,"E11"),sQuery(id+"F0.wireOp",EDGE,"E12"),subQ1,sQuery(id+"F0.wireOp",EDGE,"E14"),subQ0])],"isStart":false})],"blendedInto":[makeQuery(id+"F1.opExtrude","CAP_FACE",FACE,{"disambiguationData":[OSD([sQuery(id+"F0.wireOp",EDGE,"E0"),sQuery(id+"F0.wireOp",EDGE,"E1"),sQuery(id+"F0.wireOp",EDGE,"E2"),sQuery(id+"F0.wireOp",EDGE,"E3"),sQuery(id+"F0.wireOp",EDGE,"E4.MirrorCS"),sQuery(id+"F0.wireOp",EDGE,"E5.MirrorCS"),sQuery(id+"F0.wireOp",EDGE,"E6.MirrorCS"),sQuery(id+"F0.wireOp",EDGE,"E7"),sQuery(id+"F0.wireOp",EDGE,"E8"),sQuery(id+"F0.wireOp",EDGE,"E9"),sQuery(id+"F0.wireOp",EDGE,"E10"),sQuery(id+"F0.wireOp",EDGE,"E11"),sQuery(id+"F0.wireOp",EDGE,"E12"),subQ1,sQuery(id+"F0.wireOp",EDGE,"E14"),subQ0])],"isStart":false})]});}
            var Q17;
            {var subQ0=sQuery(id+"F0.wireOp",EDGE,"E15");var subQ1=sQuery(id+"F0.wireOp",EDGE,"E13");Q17=makeQuery(id+"F4.opFillet","BLEND_EDGE",EDGE,{"blendedFrom":[makeQuery(id+"F3.opChamfer","BLEND_EDGE",EDGE,{"blendedFrom":[makeQuery(id+"F1.opExtrude","SWEPT_EDGE",EDGE,{"disambiguationData":[OSD([subQ1,subQ0])]}),makeQuery(id+"F1.opExtrude","SWEPT_FACE",FACE,{"disambiguationData":[OSD([subQ1])]})],"blendedInto":[makeQuery(id+"F1.opExtrude","SWEPT_FACE",FACE,{"disambiguationData":[OSD([subQ1])]})]}),makeQuery(id+"F1.opExtrude","CAP_FACE",FACE,{"disambiguationData":[OSD([sQuery(id+"F0.wireOp",EDGE,"E0"),sQuery(id+"F0.wireOp",EDGE,"E1"),sQuery(id+"F0.wireOp",EDGE,"E2"),sQuery(id+"F0.wireOp",EDGE,"E3"),sQuery(id+"F0.wireOp",EDGE,"E4.MirrorCS"),sQuery(id+"F0.wireOp",EDGE,"E5.MirrorCS"),sQuery(id+"F0.wireOp",EDGE,"E6.MirrorCS"),sQuery(id+"F0.wireOp",EDGE,"E7"),sQuery(id+"F0.wireOp",EDGE,"E8"),sQuery(id+"F0.wireOp",EDGE,"E9"),sQuery(id+"F0.wireOp",EDGE,"E10"),sQuery(id+"F0.wireOp",EDGE,"E11"),sQuery(id+"F0.wireOp",EDGE,"E12"),subQ1,sQuery(id+"F0.wireOp",EDGE,"E14"),subQ0])],"isStart":false})],"blendedInto":[makeQuery(id+"F1.opExtrude","CAP_FACE",FACE,{"disambiguationData":[OSD([sQuery(id+"F0.wireOp",EDGE,"E0"),sQuery(id+"F0.wireOp",EDGE,"E1"),sQuery(id+"F0.wireOp",EDGE,"E2"),sQuery(id+"F0.wireOp",EDGE,"E3"),sQuery(id+"F0.wireOp",EDGE,"E4.MirrorCS"),sQuery(id+"F0.wireOp",EDGE,"E5.MirrorCS"),sQuery(id+"F0.wireOp",EDGE,"E6.MirrorCS"),sQuery(id+"F0.wireOp",EDGE,"E7"),sQuery(id+"F0.wireOp",EDGE,"E8"),sQuery(id+"F0.wireOp",EDGE,"E9"),sQuery(id+"F0.wireOp",EDGE,"E10"),sQuery(id+"F0.wireOp",EDGE,"E11"),sQuery(id+"F0.wireOp",EDGE,"E12"),subQ1,sQuery(id+"F0.wireOp",EDGE,"E14"),subQ0])],"isStart":false})]});}
            fillet(context, id + "F15", {"entities" : qUnion([Q0, Q1, Q2, Q3, Q4, Q5, Q6, Q7, Q8, Q9, Q10, Q11, Q12, Q13, Q14, Q15, Q16, Q17]), "radius" : 5 * mm, "allowEdgeOverflow" : false});
        }
        {
            var Q0;
            {var subQ0=sQuery(id+"F0.wireOp",EDGE,"E4.MirrorCS");Q0=makeQuery(id+"F12.opFillet","BLEND_EDGE",EDGE,{"blendedFrom":[makeQuery(id+"F1.opExtrude","SWEPT_EDGE",EDGE,{"disambiguationData":[OSD([subQ0,sQuery(id+"F0.wireOp",EDGE,"E5.MirrorCS")])]}),makeQuery(id+"F8.opFillet","BLEND_FACE",FACE,{"disambiguationData":[OSD([subQ0,sQuery(id+"F0.wireOp",EDGE,"E8"),sQuery(id+"F0.wireOp",EDGE,"E11")])]})],"blendedInto":[makeQuery(id+"F8.opFillet","BLEND_FACE",FACE,{"disambiguationData":[OSD([subQ0,sQuery(id+"F0.wireOp",EDGE,"E8"),sQuery(id+"F0.wireOp",EDGE,"E11")])]})]});}
            var Q1;
            {var subQ0=sQuery(id+"F0.wireOp",EDGE,"E5.MirrorCS");var subQ1=sQuery(id+"F0.wireOp",EDGE,"E4.MirrorCS");Q1=makeQuery(id+"F12.opFillet","BLEND_EDGE",EDGE,{"blendedFrom":[makeQuery(id+"F1.opExtrude","SWEPT_EDGE",EDGE,{"disambiguationData":[OSD([subQ1,subQ0])]}),makeQuery(id+"F8.opFillet","SPLIT",FACE,{"disambiguationData":[OD(2.0)],"derivedFrom":makeQuery(id+"F1.opExtrude","CAP_FACE",FACE,{"disambiguationData":[OSD([sQuery(id+"F0.wireOp",EDGE,"E0"),sQuery(id+"F0.wireOp",EDGE,"E1"),sQuery(id+"F0.wireOp",EDGE,"E2"),sQuery(id+"F0.wireOp",EDGE,"E3"),subQ1,subQ0,sQuery(id+"F0.wireOp",EDGE,"E6.MirrorCS"),sQuery(id+"F0.wireOp",EDGE,"E7"),sQuery(id+"F0.wireOp",EDGE,"E8"),sQuery(id+"F0.wireOp",EDGE,"E9"),sQuery(id+"F0.wireOp",EDGE,"E10"),sQuery(id+"F0.wireOp",EDGE,"E11"),sQuery(id+"F0.wireOp",EDGE,"E12"),sQuery(id+"F0.wireOp",EDGE,"E13"),sQuery(id+"F0.wireOp",EDGE,"E14"),sQuery(id+"F0.wireOp",EDGE,"E15")])],"isStart":true})})],"blendedInto":[makeQuery(id+"F8.opFillet","SPLIT",FACE,{"disambiguationData":[OD(2.0)],"derivedFrom":makeQuery(id+"F1.opExtrude","CAP_FACE",FACE,{"disambiguationData":[OSD([sQuery(id+"F0.wireOp",EDGE,"E0"),sQuery(id+"F0.wireOp",EDGE,"E1"),sQuery(id+"F0.wireOp",EDGE,"E2"),sQuery(id+"F0.wireOp",EDGE,"E3"),subQ1,subQ0,sQuery(id+"F0.wireOp",EDGE,"E6.MirrorCS"),sQuery(id+"F0.wireOp",EDGE,"E7"),sQuery(id+"F0.wireOp",EDGE,"E8"),sQuery(id+"F0.wireOp",EDGE,"E9"),sQuery(id+"F0.wireOp",EDGE,"E10"),sQuery(id+"F0.wireOp",EDGE,"E11"),sQuery(id+"F0.wireOp",EDGE,"E12"),sQuery(id+"F0.wireOp",EDGE,"E13"),sQuery(id+"F0.wireOp",EDGE,"E14"),sQuery(id+"F0.wireOp",EDGE,"E15")])],"isStart":true})})]});}
            var Q2;
            Q2=makeQuery(id+"F1.opExtrude","CAP_EDGE",EDGE,{"disambiguationData":[OSD([sQuery(id+"F0.wireOp",EDGE,"E5.MirrorCS")])],"isStart":true});
            var Q3;
            Q3=makeQuery(id+"F1.opExtrude","CAP_EDGE",EDGE,{"disambiguationData":[OSD([sQuery(id+"F0.wireOp",EDGE,"E2")])],"isStart":true});
            var Q4;
            {var subQ0=sQuery(id+"F0.wireOp",EDGE,"E2");var subQ1=sQuery(id+"F0.wireOp",EDGE,"E1");Q4=makeQuery(id+"F13.opFillet","BLEND_EDGE",EDGE,{"blendedFrom":[makeQuery(id+"F1.opExtrude","SWEPT_EDGE",EDGE,{"disambiguationData":[OSD([subQ1,subQ0])]}),makeQuery(id+"F8.opFillet","SPLIT",FACE,{"disambiguationData":[OD(2.0)],"derivedFrom":makeQuery(id+"F1.opExtrude","CAP_FACE",FACE,{"disambiguationData":[OSD([sQuery(id+"F0.wireOp",EDGE,"E0"),subQ1,subQ0,sQuery(id+"F0.wireOp",EDGE,"E3"),sQuery(id+"F0.wireOp",EDGE,"E4.MirrorCS"),sQuery(id+"F0.wireOp",EDGE,"E5.MirrorCS"),sQuery(id+"F0.wireOp",EDGE,"E6.MirrorCS"),sQuery(id+"F0.wireOp",EDGE,"E7"),sQuery(id+"F0.wireOp",EDGE,"E8"),sQuery(id+"F0.wireOp",EDGE,"E9"),sQuery(id+"F0.wireOp",EDGE,"E10"),sQuery(id+"F0.wireOp",EDGE,"E11"),sQuery(id+"F0.wireOp",EDGE,"E12"),sQuery(id+"F0.wireOp",EDGE,"E13"),sQuery(id+"F0.wireOp",EDGE,"E14"),sQuery(id+"F0.wireOp",EDGE,"E15")])],"isStart":true})})],"blendedInto":[makeQuery(id+"F8.opFillet","SPLIT",FACE,{"disambiguationData":[OD(2.0)],"derivedFrom":makeQuery(id+"F1.opExtrude","CAP_FACE",FACE,{"disambiguationData":[OSD([sQuery(id+"F0.wireOp",EDGE,"E0"),subQ1,subQ0,sQuery(id+"F0.wireOp",EDGE,"E3"),sQuery(id+"F0.wireOp",EDGE,"E4.MirrorCS"),sQuery(id+"F0.wireOp",EDGE,"E5.MirrorCS"),sQuery(id+"F0.wireOp",EDGE,"E6.MirrorCS"),sQuery(id+"F0.wireOp",EDGE,"E7"),sQuery(id+"F0.wireOp",EDGE,"E8"),sQuery(id+"F0.wireOp",EDGE,"E9"),sQuery(id+"F0.wireOp",EDGE,"E10"),sQuery(id+"F0.wireOp",EDGE,"E11"),sQuery(id+"F0.wireOp",EDGE,"E12"),sQuery(id+"F0.wireOp",EDGE,"E13"),sQuery(id+"F0.wireOp",EDGE,"E14"),sQuery(id+"F0.wireOp",EDGE,"E15")])],"isStart":true})})]});}
            var Q5;
            {var subQ0=sQuery(id+"F0.wireOp",EDGE,"E1");Q5=makeQuery(id+"F13.opFillet","BLEND_EDGE",EDGE,{"blendedFrom":[makeQuery(id+"F1.opExtrude","SWEPT_EDGE",EDGE,{"disambiguationData":[OSD([subQ0,sQuery(id+"F0.wireOp",EDGE,"E2")])]}),makeQuery(id+"F8.opFillet","BLEND_FACE",FACE,{"disambiguationData":[OSD([subQ0,sQuery(id+"F0.wireOp",EDGE,"E7"),sQuery(id+"F0.wireOp",EDGE,"E10")])]})],"blendedInto":[makeQuery(id+"F8.opFillet","BLEND_FACE",FACE,{"disambiguationData":[OSD([subQ0,sQuery(id+"F0.wireOp",EDGE,"E7"),sQuery(id+"F0.wireOp",EDGE,"E10")])]})]});}
            fillet(context, id + "F16", {"entities" : qUnion([Q0, Q1, Q2, Q3, Q4, Q5]), "radius" : 5 * mm, "allowEdgeOverflow" : false});
        }
    });
